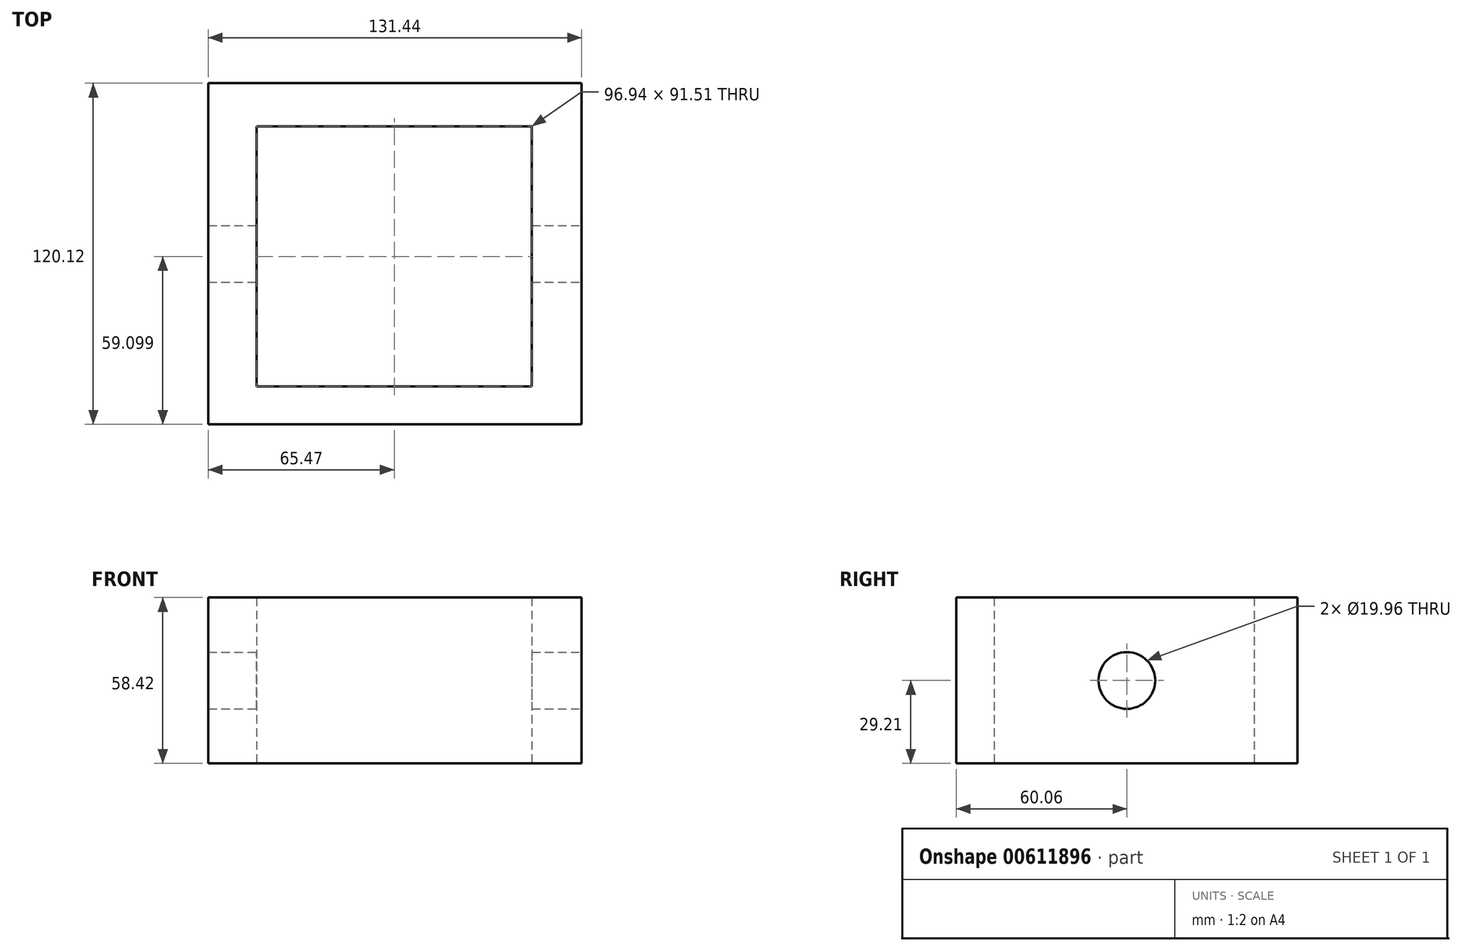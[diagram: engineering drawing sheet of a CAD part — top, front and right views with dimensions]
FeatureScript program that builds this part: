
annotation { "Feature Type Name" : "Feature", "Feature Type Description" : "" }
export const myFeature = defineFeature(function(context is Context, id is Id, definition is map)
    precondition{}
    {
        {
            var Q0;
            Q0=qCreatedBy(makeId("Top.planeOp"),FACE);
            var sketch = newSketch(context, id + "F0", { "sketchPlane" : qUnion([Q0])});
            skLineSegment(sketch, "E0.bottom", {"start": v(65.72, 60.06) * mm, "end": v(-65.72, 60.06) * mm});
            skLineSegment(sketch, "E0.top", {"start": v(65.72, -60.06) * mm, "end": v(-65.72, -60.06) * mm});
            skLineSegment(sketch, "E0.left", {"start": v(65.72, 60.06) * mm, "end": v(65.72, -60.06) * mm});
            skLineSegment(sketch, "E0.right", {"start": v(-65.72, 60.06) * mm, "end": v(-65.72, -60.06) * mm});
            skPoint(sketch, "E0.middle", {"position": v(0, 0) * mm});
            skSolve(sketch);
        }
        {
            var Q0;
            Q0=makeQuery(id+"F0.imprint","IMPRINT",FACE,{"disambiguationData":[TD([[makeQuery(id+"F0.imprint","IMPRINT",EDGE,{"derivedFrom":sQuery(id+"F0.wireOp",EDGE,"E0.bottom")}),1.0]])]});
            extrude(context, id + "F1", {"entities" : qUnion([Q0]), "depth" : 58.42 * mm, "offsetDistance" : 25.4 * mm});
        }
        {
            var Q0;
            Q0=makeQuery(id+"F1.opExtrude","SWEPT_FACE",FACE,{"disambiguationData":[OSD([sQuery(id+"F0.wireOp",EDGE,"E0.left")])]});
            var sketch = newSketch(context, id + "F2", { "sketchPlane" : qUnion([Q0])});
            skLineSegment(sketch, "E1", {"start": v(0, 58.42) * mm, "end": v(0, 0) * mm, "construction": true});
            skLineSegment(sketch, "E2", {"start": v(-60.06, 29.21) * mm, "end": v(60.06, 29.21) * mm, "construction": true});
            skCircle(sketch, "E3", {"center": v(0, 29.21) * mm, "radius": 9.98 * mm});
            skSolve(sketch);
        }
        {
            var Q0;
            Q0=makeQuery(id+"F2.imprint","IMPRINT",FACE,{"disambiguationData":[TD([[makeQuery(id+"F2.imprint","IMPRINT",EDGE,{"derivedFrom":sQuery(id+"F2.wireOp",EDGE,"E3")}),1.0]])]});
            var sketch = newSketch(context, id + "F3", { "sketchPlane" : qUnion([Q0])});
            skSolve(sketch);
        }
        {
            var Q0;
            Q0 = qSketchRegion(id + "F3", true);
            var Q1;
            Q1=makeQuery(id+"F2.imprint","IMPRINT",FACE,{"disambiguationData":[TD([[makeQuery(id+"F2.imprint","IMPRINT",EDGE,{"derivedFrom":sQuery(id+"F2.wireOp",EDGE,"E3")}),1.0]])]});
            extrude(context, id + "F4", {"entities" : qUnion([Q0, Q1]), "operationType" : NewBodyOperationType.REMOVE, "endBound" : BoundingType.SYMMETRIC, "oppositeDirection" : true, "depth" : 314.45 * mm, "offsetDistance" : 25.4 * mm});
        }
        {
            var Q0;
            Q0=qCreatedBy(makeId("Top.planeOp"),FACE);
            var sketch = newSketch(context, id + "F5", { "sketchPlane" : qUnion([Q0])});
            skLineSegment(sketch, "E4", {"start": v(-48.72, 44.8) * mm, "end": v(-48.72, -46.71) * mm});
            skLineSegment(sketch, "E5", {"start": v(-48.72, -46.71) * mm, "end": v(48.22, -46.71) * mm});
            skLineSegment(sketch, "E6", {"start": v(48.22, -46.71) * mm, "end": v(48.22, 44.8) * mm});
            skLineSegment(sketch, "E7", {"start": v(48.22, 44.8) * mm, "end": v(-48.72, 44.8) * mm});
            skSolve(sketch);
        }
        {
            var Q0;
            Q0 = qSketchRegion(id + "F5", true);
            extrude(context, id + "F6", {"entities" : qUnion([Q0]), "operationType" : NewBodyOperationType.REMOVE, "endBound" : BoundingType.SYMMETRIC, "depth" : 258.06 * mm, "offsetDistance" : 25.4 * mm});
        }
    });
